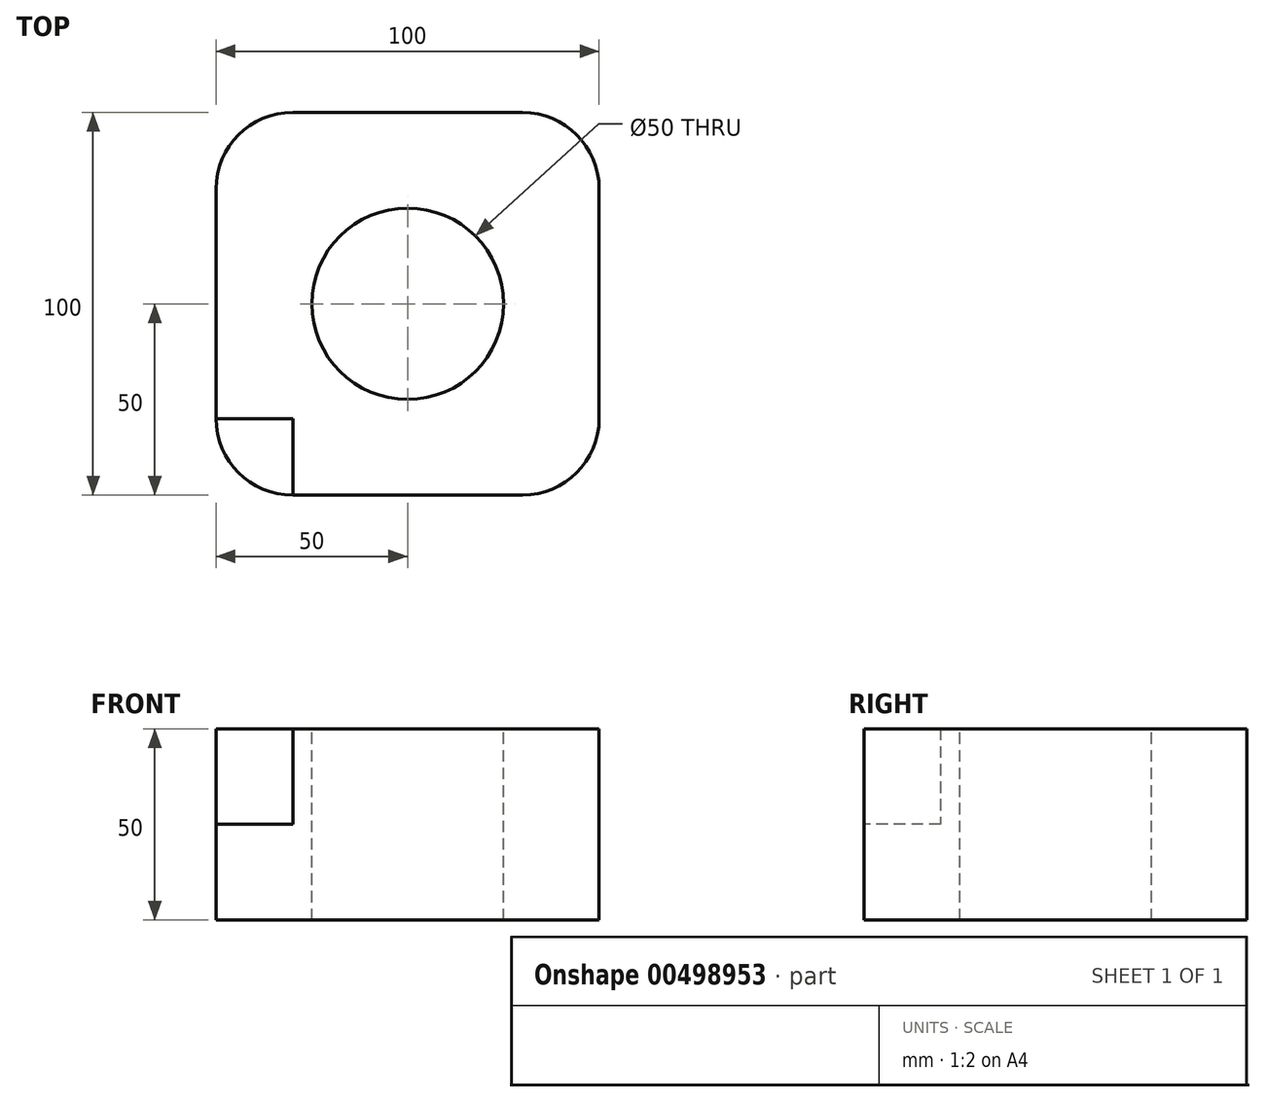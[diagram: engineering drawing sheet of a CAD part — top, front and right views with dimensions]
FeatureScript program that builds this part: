
annotation { "Feature Type Name" : "Feature", "Feature Type Description" : "" }
export const myFeature = defineFeature(function(context is Context, id is Id, definition is map)
    precondition{}
    {
        {
            var Q0;
            Q0=qCreatedBy(makeId("Top.planeOp"),FACE);
            var sketch = newSketch(context, id + "F0", { "sketchPlane" : qUnion([Q0])});
            skLineSegment(sketch, "E0.bottom", {"start": v(30, 50) * mm, "end": v(-30, 50) * mm});
            skLineSegment(sketch, "E0.top", {"start": v(30, -50) * mm, "end": v(-30, -50) * mm});
            skLineSegment(sketch, "E0.left", {"start": v(50, 30) * mm, "end": v(50, -30) * mm});
            skLineSegment(sketch, "E0.right", {"start": v(-50, 30) * mm, "end": v(-50, -30) * mm});
            skPoint(sketch, "E0.middle", {"position": v(0, 0) * mm});
            skPoint(sketch, "E1.visualSharp", {"position": v(50, 50) * mm});
            skArc(sketch, "E1.filletArc", {"start": v(50, 30) * mm, "mid": v(44.14, 44.14) * mm, "end": v(30, 50) * mm});
            skPoint(sketch, "E2.visualSharp", {"position": v(50, -50) * mm});
            skArc(sketch, "E2.filletArc", {"start": v(30, -50) * mm, "mid": v(44.14, -44.14) * mm, "end": v(50, -30) * mm});
            skPoint(sketch, "E3.visualSharp", {"position": v(-50, 50) * mm});
            skArc(sketch, "E3.filletArc", {"start": v(-30, 50) * mm, "mid": v(-44.14, 44.14) * mm, "end": v(-50, 30) * mm});
            skPoint(sketch, "E4.visualSharp", {"position": v(-50, -50) * mm});
            skArc(sketch, "E4.filletArc", {"start": v(-50, -30) * mm, "mid": v(-44.14, -44.14) * mm, "end": v(-30, -50) * mm});
            skSolve(sketch);
        }
        {
            var Q0;
            Q0=makeQuery(id+"F0.imprint","IMPRINT",FACE,{"disambiguationData":[TD([[makeQuery(id+"F0.imprint","IMPRINT",EDGE,{"derivedFrom":sQuery(id+"F0.wireOp",EDGE,"E0.bottom")}),1.0]])]});
            extrude(context, id + "F1", {"entities" : qUnion([Q0]), "depth" : 50 * mm});
        }
        {
            var Q0;
            Q0=makeQuery(id+"F1.opExtrude","CAP_FACE",FACE,{"disambiguationData":[OSD([sQuery(id+"F0.wireOp",EDGE,"E0.bottom"),sQuery(id+"F0.wireOp",EDGE,"E0.top"),sQuery(id+"F0.wireOp",EDGE,"E0.left"),sQuery(id+"F0.wireOp",EDGE,"E0.right")])],"isStart":false});
            var sketch = newSketch(context, id + "F2", { "sketchPlane" : qUnion([Q0])});
            skCircle(sketch, "E5", {"center": v(0, 0) * mm, "radius": 25 * mm});
            skSolve(sketch);
        }
        {
            var Q0;
            Q0=makeQuery(id+"F2.imprint","IMPRINT",FACE,{"disambiguationData":[TD([[makeQuery(id+"F2.imprint","IMPRINT",EDGE,{"derivedFrom":sQuery(id+"F2.wireOp",EDGE,"E5")}),1.0]])]});
            extrude(context, id + "F3", {"entities" : qUnion([Q0]), "operationType" : NewBodyOperationType.REMOVE, "endBound" : BoundingType.THROUGH_ALL, "oppositeDirection" : true, "depth" : 25 * mm});
        }
        {
            var Q0;
            Q0=makeQuery(id+"F1.opExtrude","CAP_FACE",FACE,{"disambiguationData":[OSD([sQuery(id+"F0.wireOp",EDGE,"E0.bottom"),sQuery(id+"F0.wireOp",EDGE,"E0.top"),sQuery(id+"F0.wireOp",EDGE,"E0.left"),sQuery(id+"F0.wireOp",EDGE,"E0.right"),sQuery(id+"F0.wireOp",EDGE,"E1.filletArc"),sQuery(id+"F0.wireOp",EDGE,"E2.filletArc"),sQuery(id+"F0.wireOp",EDGE,"E3.filletArc"),sQuery(id+"F0.wireOp",EDGE,"E4.filletArc")])],"isStart":false});
            var sketch = newSketch(context, id + "F4", { "sketchPlane" : qUnion([Q0])});
            skPoint(sketch, "E6.middle", {"position": v(-50, -30) * mm});
            skLineSegment(sketch, "E7.bottom", {"start": v(-50, -30) * mm, "end": v(-30, -30) * mm});
            skLineSegment(sketch, "E7.top", {"start": v(-50, -50) * mm, "end": v(-30, -50) * mm});
            skLineSegment(sketch, "E7.left", {"start": v(-50, -30) * mm, "end": v(-50, -50) * mm});
            skLineSegment(sketch, "E7.right", {"start": v(-30, -30) * mm, "end": v(-30, -50) * mm});
            skSolve(sketch);
        }
        {
            var Q0;
            Q0=makeQuery(id+"F4.imprint","IMPRINT",FACE,{"disambiguationData":[TD([[makeQuery(id+"F4.imprint","IMPRINT",EDGE,{"derivedFrom":sQuery(id+"F4.wireOp",EDGE,"E7.bottom")}),-1.0]])]});
            extrude(context, id + "F5", {"entities" : qUnion([Q0]), "operationType" : NewBodyOperationType.REMOVE, "oppositeDirection" : true, "depth" : 25 * mm});
        }
    });
